# Revit family: SH-16102
name_source: partatom
category: Lighting Fixtures
revit_build: Autodesk Revit 2017 (Build: 20160225_1515(x64)
units: mm (PartAtom-declared; Revit-internal decimal feet)

## family parameters
Cut with Voids When Loaded = No
Host = Face
Light Source = Yes
Part Type = Normal
Room Calculation Point = No
Round Connector Dimension = Use Diameter
Shared = No

## types (1)
- SH-16102(Black color-3000K-E27)
    Body Material = Aluminum
    Body color = Black Body
    Color Filter = 16777215
    Default Elevation = 122 cm
    Diffuser Material = Polycarbonate-anti uv
    Dimming Lamp Color Temperature Shift = <None>
    Emit Shape Visible in Rendering = No
    Emit from Circle Diameter = 20 cm
    Height = 60 cm
    IP = IP65
    Lamp = E27
    Length = 24 cm
    Light Source Symbol Size = 60 cm
    Manufacturer = SHOA
    Model = SH-16102
    Protection Class = Class I
    URL = https://www.shoaco.com
    Voltage/Frequency = 230v/50hz
    Wattage. = 12 W
    Width = 24 cm
    color temperature = 3000K
    consumption current = 0 A
    website = www.shoaco.com

## geometry (parser evidence)
native form markers: Sweep x3
no freeform markers — native parametric forms only
